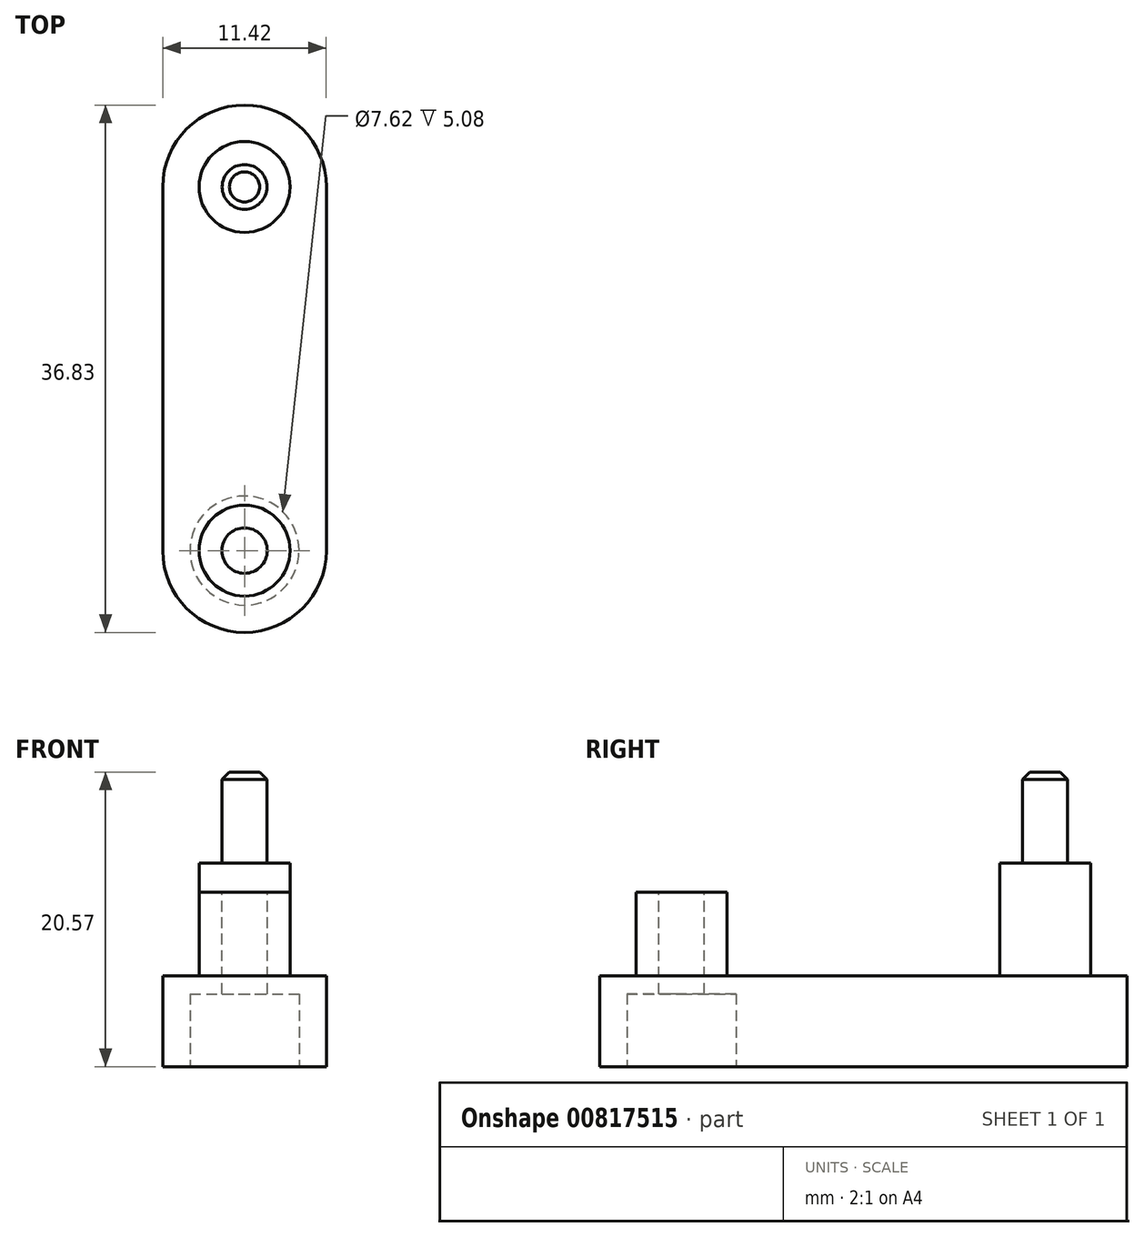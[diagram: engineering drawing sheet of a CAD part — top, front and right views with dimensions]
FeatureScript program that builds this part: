
annotation { "Feature Type Name" : "Feature", "Feature Type Description" : "" }
export const myFeature = defineFeature(function(context is Context, id is Id, definition is map)
    precondition{}
    {
        {
            var Q0;
            Q0=qCreatedBy(makeId("Top.planeOp"),FACE);
            var sketch = newSketch(context, id + "F0", { "sketchPlane" : qUnion([Q0])});
            skLineSegment(sketch, "E0.left", {"start": v(-5.72, 14.16) * mm, "end": v(-5.72, -11.23) * mm});
            skLineSegment(sketch, "E0.right", {"start": v(5.72, 14.16) * mm, "end": v(5.72, -11.23) * mm});
            skArc(sketch, "E1", {"start": v(5.72, 14.16) * mm, "mid": v(0, 19.88) * mm, "end": v(-5.72, 14.16) * mm});
            skPoint(sketch, "E1.first.point", {"position": v(-5.71, 14.16) * mm});
            skPoint(sketch, "E1.second.point", {"position": v(5.71, 14.16) * mm});
            skPoint(sketch, "E1.third.point", {"position": v(-0.26, 8.45) * mm});
            skArc(sketch, "E2", {"start": v(-5.72, -11.23) * mm, "mid": v(0, -16.95) * mm, "end": v(5.72, -11.23) * mm});
            skPoint(sketch, "E2.first.point", {"position": v(-5.72, -11.23) * mm});
            skPoint(sketch, "E2.second.point", {"position": v(5.72, -11.23) * mm});
            skPoint(sketch, "E2.third.point", {"position": v(0, -16.95) * mm});
            skSolve(sketch);
        }
        {
            var Q0;
            Q0 = qSketchRegion(id + "F0", true);
            extrude(context, id + "F1", {"entities" : qUnion([Q0]), "depth" : 6.35 * mm, "offsetDistance" : 25.4 * mm});
        }
        {
            var Q0;
            Q0=makeQuery(id+"F1.opExtrude","CAP_FACE",FACE,{"disambiguationData":[OSD([sQuery(id+"F0.wireOp",EDGE,"E0.left"),sQuery(id+"F0.wireOp",EDGE,"E0.right"),sQuery(id+"F0.wireOp",EDGE,"E1"),sQuery(id+"F0.wireOp",EDGE,"E2")])],"isStart":false});
            var sketch = newSketch(context, id + "F2", { "sketchPlane" : qUnion([Q0])});
            skCircle(sketch, "E3", {"center": v(0, 14.16) * mm, "radius": 3.18 * mm});
            skSolve(sketch);
        }
        {
            var Q0;
            Q0 = qSketchRegion(id + "F2", true);
            extrude(context, id + "F3", {"entities" : qUnion([Q0]), "operationType" : NewBodyOperationType.ADD, "depth" : 7.87 * mm, "offsetDistance" : 25.4 * mm});
        }
        {
            var Q0;
            Q0=makeQuery(id+"F3.opExtrude","CAP_FACE",FACE,{"disambiguationData":[OSD([sQuery(id+"F2.wireOp",EDGE,"E3")])],"isStart":false});
            var sketch = newSketch(context, id + "F4", { "sketchPlane" : qUnion([Q0])});
            skCircle(sketch, "E4", {"center": v(0, 14.16) * mm, "radius": 1.56 * mm});
            skSolve(sketch);
        }
        {
            var Q0;
            Q0 = qSketchRegion(id + "F4", true);
            extrude(context, id + "F5", {"entities" : qUnion([Q0]), "operationType" : NewBodyOperationType.ADD, "depth" : 6.35 * mm, "offsetDistance" : 25.4 * mm});
        }
        {
            var Q0;
            Q0=makeQuery(id+"F5.opExtrude","CAP_EDGE",EDGE,{"disambiguationData":[OSD([sQuery(id+"F4.wireOp",EDGE,"E4")])],"isStart":false});
            chamfer(context, id + "F6", {"entities" : qUnion([Q0]), "width" : 0.5 * mm, "tangentPropagation" : true});
        }
        {
            var Q0;
            Q0=makeQuery(id+"F1.opExtrude","CAP_FACE",FACE,{"disambiguationData":[OSD([sQuery(id+"F0.wireOp",EDGE,"E0.left"),sQuery(id+"F0.wireOp",EDGE,"E0.right"),sQuery(id+"F0.wireOp",EDGE,"E1"),sQuery(id+"F0.wireOp",EDGE,"E2")])],"isStart":false});
            var sketch = newSketch(context, id + "F7", { "sketchPlane" : qUnion([Q0])});
            skCircle(sketch, "E5", {"center": v(0, -11.23) * mm, "radius": 3.18 * mm});
            skSolve(sketch);
        }
        {
            var Q0;
            Q0 = qSketchRegion(id + "F7", true);
            extrude(context, id + "F8", {"entities" : qUnion([Q0]), "operationType" : NewBodyOperationType.ADD, "depth" : 5.84 * mm, "offsetDistance" : 25.4 * mm});
        }
        {
            var Q0;
            Q0=makeQuery(id+"F8.opExtrude","CAP_FACE",FACE,{"disambiguationData":[OSD([sQuery(id+"F7.wireOp",EDGE,"E5")])],"isStart":false});
            var sketch = newSketch(context, id + "F9", { "sketchPlane" : qUnion([Q0])});
            skCircle(sketch, "E6", {"center": v(0, -11.23) * mm, "radius": 1.59 * mm});
            skSolve(sketch);
        }
        {
            var Q0;
            Q0 = qSketchRegion(id + "F9", true);
            extrude(context, id + "F10", {"entities" : qUnion([Q0]), "operationType" : NewBodyOperationType.REMOVE, "endBound" : BoundingType.THROUGH_ALL, "oppositeDirection" : true, "depth" : 25.4 * mm, "offsetDistance" : 25.4 * mm});
        }
        {
            var Q0;
            Q0=makeQuery(id+"F1.opExtrude","CAP_FACE",FACE,{"disambiguationData":[OSD([sQuery(id+"F0.wireOp",EDGE,"E0.left"),sQuery(id+"F0.wireOp",EDGE,"E0.right"),sQuery(id+"F0.wireOp",EDGE,"E1"),sQuery(id+"F0.wireOp",EDGE,"E2")])],"isStart":true});
            var sketch = newSketch(context, id + "F11", { "sketchPlane" : qUnion([Q0])});
            skCircle(sketch, "E7", {"center": v(0, 11.23) * mm, "radius": 3.81 * mm});
            skSolve(sketch);
        }
        {
            var Q0;
            Q0 = qSketchRegion(id + "F11", true);
            extrude(context, id + "F12", {"entities" : qUnion([Q0]), "operationType" : NewBodyOperationType.REMOVE, "oppositeDirection" : true, "depth" : 5.08 * mm, "offsetDistance" : 25.4 * mm});
        }
    });
